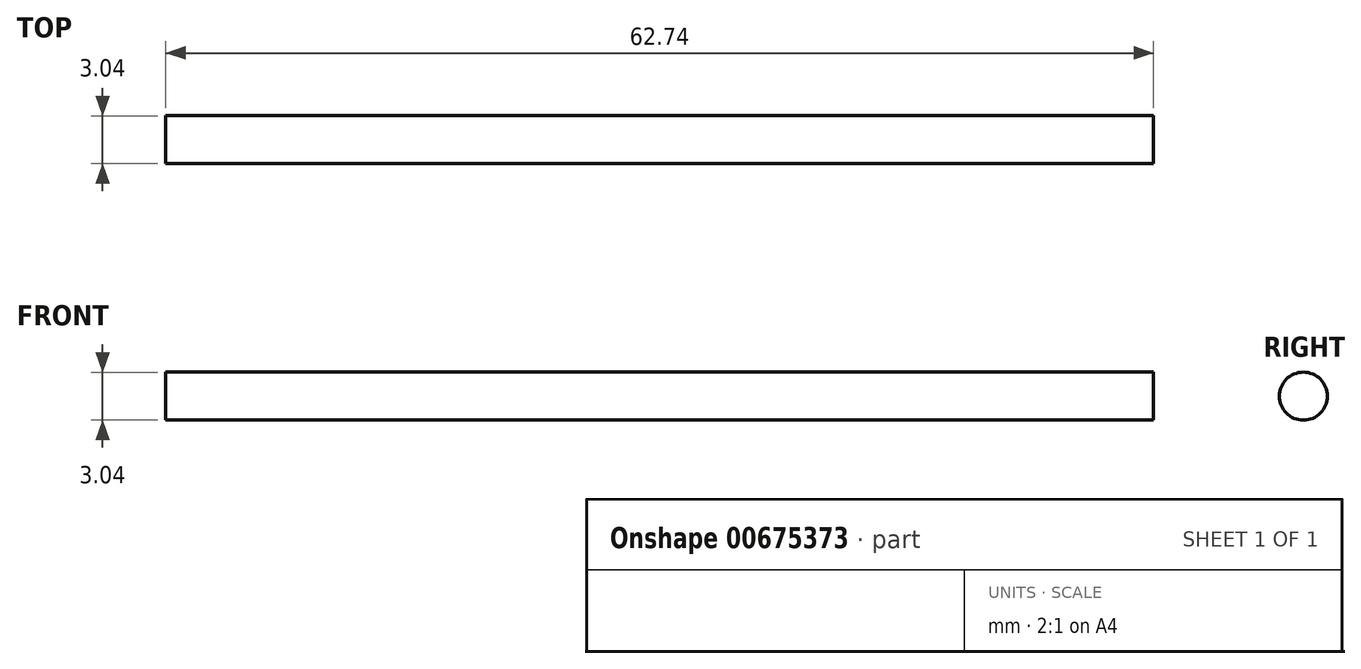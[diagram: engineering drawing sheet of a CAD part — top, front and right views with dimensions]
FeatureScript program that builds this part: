
annotation { "Feature Type Name" : "Feature", "Feature Type Description" : "" }
export const myFeature = defineFeature(function(context is Context, id is Id, definition is map)
    precondition{}
    {
        {
            var Q0;
            Q0=qCreatedBy(makeId("Right.planeOp"),FACE);
            var sketch = newSketch(context, id + "F0", { "sketchPlane" : qUnion([Q0])});
            skCircle(sketch, "E0", {"center": v(0, 0) * mm, "radius": 1.52 * mm});
            skSolve(sketch);
        }
        {
            var Q0;
            Q0 = qSketchRegion(id + "F0", true);
            extrude(context, id + "F1", {"entities" : qUnion([Q0]), "depth" : 62.74 * mm, "offsetDistance" : 25.4 * mm});
        }
    });
